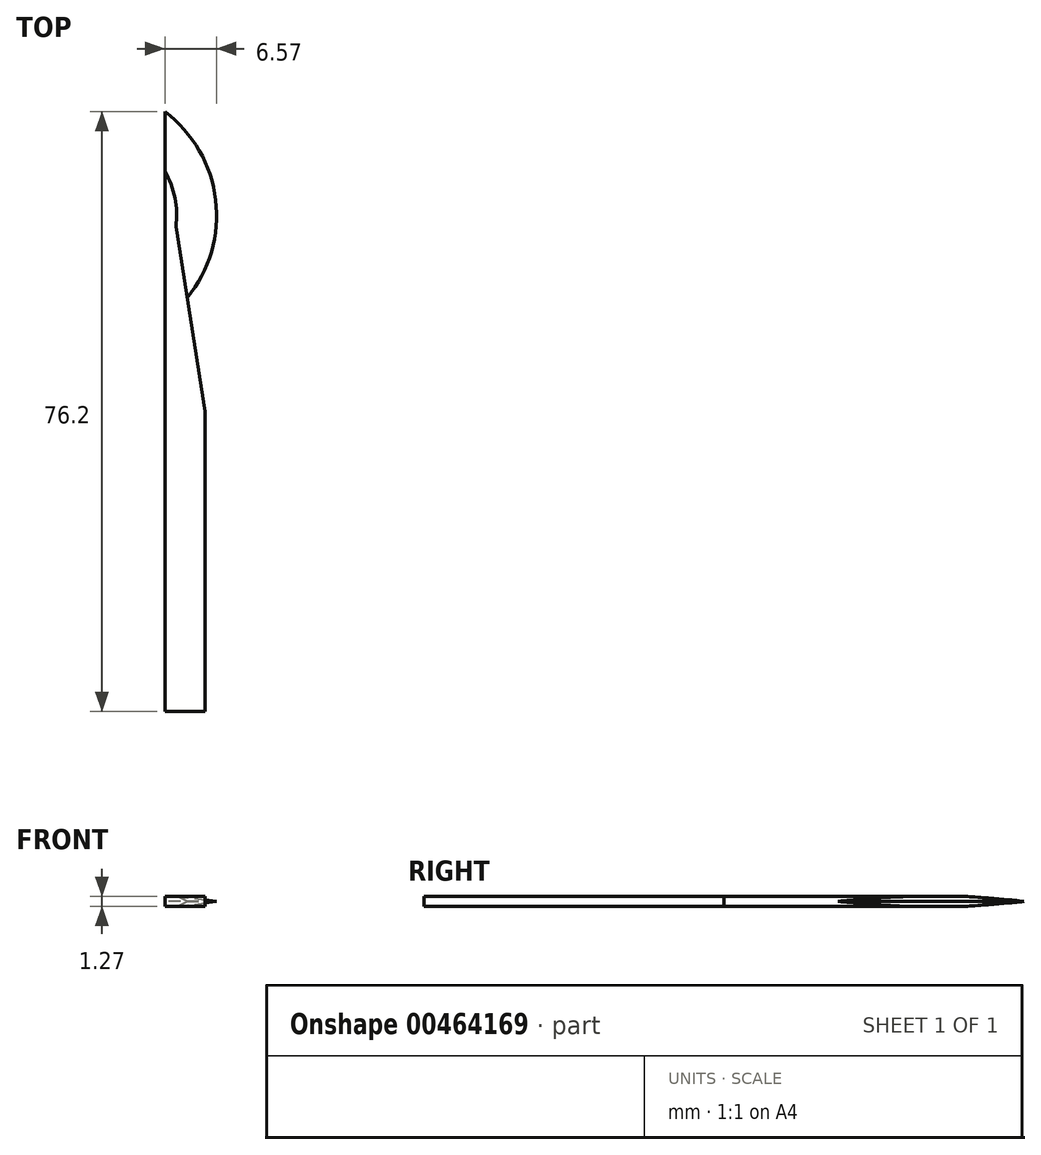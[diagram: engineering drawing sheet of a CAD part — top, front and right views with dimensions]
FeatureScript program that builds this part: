
annotation { "Feature Type Name" : "Feature", "Feature Type Description" : "" }
export const myFeature = defineFeature(function(context is Context, id is Id, definition is map)
    precondition{}
    {
        {
            var Q0;
            Q0=qCreatedBy(makeId("Top.planeOp"),FACE);
            var sketch = newSketch(context, id + "F0", { "sketchPlane" : qUnion([Q0])});
            skLineSegment(sketch, "E0", {"start": v(-36.83, 0) * mm, "end": v(-31.75, 0) * mm});
            skLineSegment(sketch, "E1", {"start": v(-36.83, 0) * mm, "end": v(-36.83, 25.4) * mm});
            skLineSegment(sketch, "E2", {"start": v(-31.75, 0) * mm, "end": v(-31.75, 25.4) * mm});
            skLineSegment(sketch, "E3", {"start": v(-31.75, 25.4) * mm, "end": v(-31.75, 38.1) * mm});
            skLineSegment(sketch, "E4", {"start": v(-36.83, 25.4) * mm, "end": v(-36.83, 76.2) * mm});
            skLineSegment(sketch, "E5", {"start": v(-31.75, 38.1) * mm, "end": v(-34.02, 52.53) * mm});
            skArc(sketch, "E6", {"start": v(-34.02, 52.53) * mm, "mid": v(-30.37, 64.97) * mm, "end": v(-36.83, 76.2) * mm});
            skSolve(sketch);
        }
        {
            var Q0;
            Q0=makeQuery(id+"F0.imprint","IMPRINT",FACE,{"disambiguationData":[TD([[makeQuery(id+"F0.imprint","IMPRINT",EDGE,{"derivedFrom":sQuery(id+"F0.wireOp",EDGE,"E0")}),1.0]])]});
            extrude(context, id + "F1", {"entities" : qUnion([Q0]), "depth" : 1.27 * mm});
        }
        {
            var Q0;
            Q0=makeQuery(id+"F1.opExtrude","CAP_EDGE",EDGE,{"disambiguationData":[OSD([sQuery(id+"F0.wireOp",EDGE,"E6")])],"isStart":false});
            var Q1;
            Q1=makeQuery(id+"F1.opExtrude","CAP_EDGE",EDGE,{"disambiguationData":[OSD([sQuery(id+"F0.wireOp",EDGE,"E6")])],"isStart":true});
            chamfer(context, id + "F2", {"entities" : qUnion([Q0, Q1]), "chamferType" : ChamferType.TWO_OFFSETS, "width1" : 5.08 * mm, "oppositeDirection" : false, "width2" : 0.64 * mm, "tangentPropagation" : true});
        }
    });
